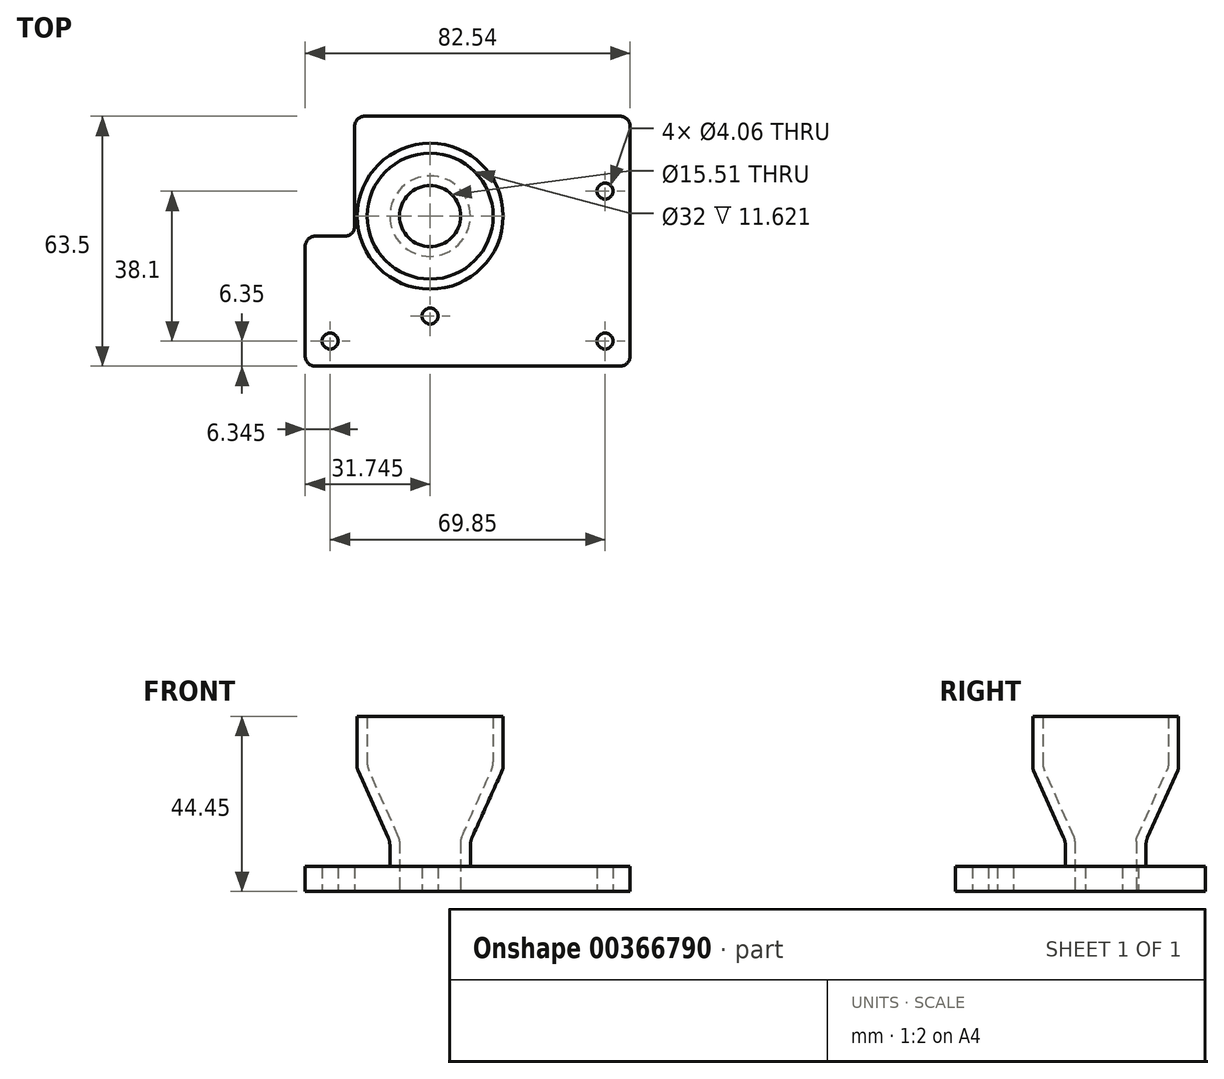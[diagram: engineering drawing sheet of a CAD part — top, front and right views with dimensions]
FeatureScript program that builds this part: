
annotation { "Feature Type Name" : "Feature", "Feature Type Description" : "" }
export const myFeature = defineFeature(function(context is Context, id is Id, definition is map)
    precondition{}
    {
        {
            var Q0;
            Q0=qCreatedBy(makeId("Top.planeOp"),FACE);
            var sketch = newSketch(context, id + "F0", { "sketchPlane" : qUnion([Q0])});
            skArc(sketch, "E0", {"start": v(-41.27, -29.21) * mm, "mid": v(-40.53, -31) * mm, "end": v(-38.73, -31.75) * mm});
            skCircle(sketch, "E1", {"center": v(-34.93, -25.4) * mm, "radius": 2.03 * mm});
            skLineSegment(sketch, "E2", {"start": v(-41.28, -1.3) * mm, "end": v(-41.28, -29.21) * mm});
            skArc(sketch, "E3", {"start": v(-38.73, 1.24) * mm, "mid": v(-40.53, 0.5) * mm, "end": v(-41.27, -1.3) * mm});
            skCircle(sketch, "E4", {"center": v(34.93, 12.7) * mm, "radius": 2.03 * mm});
            skCircle(sketch, "E5", {"center": v(34.93, -25.4) * mm, "radius": 2.03 * mm});
            skArc(sketch, "E6", {"start": v(38.74, -31.75) * mm, "mid": v(40.53, -31) * mm, "end": v(41.28, -29.21) * mm});
            skLineSegment(sketch, "E7", {"start": v(-38.73, -31.75) * mm, "end": v(38.74, -31.75) * mm});
            skCircle(sketch, "E8", {"center": v(-9.53, 6.35) * mm, "radius": 7.76 * mm});
            skLineSegment(sketch, "E9", {"start": v(41.28, -29.21) * mm, "end": v(41.28, 29.21) * mm});
            skArc(sketch, "E10", {"start": v(41.28, 29.21) * mm, "mid": v(40.53, 31) * mm, "end": v(38.74, 31.75) * mm});
            skCircle(sketch, "E11", {"center": v(-9.53, -19.05) * mm, "radius": 2.03 * mm});
            skLineSegment(sketch, "E12", {"start": v(-26.17, 31.75) * mm, "end": v(38.74, 31.75) * mm});
            skArc(sketch, "E13", {"start": v(-26.17, 31.75) * mm, "mid": v(-27.97, 31) * mm, "end": v(-28.7, 29.21) * mm});
            skLineSegment(sketch, "E14", {"start": v(-28.7, 3.78) * mm, "end": v(-28.7, 29.21) * mm});
            skLineSegment(sketch, "E15", {"start": v(-38.73, 1.24) * mm, "end": v(-31.25, 1.24) * mm});
            skArc(sketch, "E16", {"start": v(-31.25, 1.24) * mm, "mid": v(-29.45, 1.98) * mm, "end": v(-28.7, 3.78) * mm});
            skSolve(sketch);
        }
        {
            var Q0;
            Q0=makeQuery(id+"F0.imprint","IMPRINT",FACE,{"disambiguationData":[TD([[makeQuery(id+"F0.imprint","IMPRINT",EDGE,{"derivedFrom":sQuery(id+"F0.wireOp",EDGE,"E0")}),1.0]])]});
            extrude(context, id + "F1", {"entities" : qUnion([Q0]), "depth" : 6.35 * mm});
        }
        {
            var Q0;
            Q0=qCreatedBy(makeId("Top.planeOp"),FACE);
            cPlane(context, id + "F2", {"entities" : qUnion([Q0]), "cplaneType" : CPlaneType.OFFSET, "offset" : 6.35 * mm, "width" : 152.4 * mm, "height" : 152.4 * mm});
        }
        {
            var Q0;
            Q0=makeQuery(id+"F1.opExtrude","CAP_FACE",FACE,{"disambiguationData":[OSD([sQuery(id+"F0.wireOp",EDGE,"E0"),sQuery(id+"F0.wireOp",EDGE,"E1"),sQuery(id+"F0.wireOp",EDGE,"E2"),sQuery(id+"F0.wireOp",EDGE,"E3"),sQuery(id+"F0.wireOp",EDGE,"E4"),sQuery(id+"F0.wireOp",EDGE,"E5"),sQuery(id+"F0.wireOp",EDGE,"E6"),sQuery(id+"F0.wireOp",EDGE,"E7"),sQuery(id+"F0.wireOp",EDGE,"E8"),sQuery(id+"F0.wireOp",EDGE,"E9"),sQuery(id+"F0.wireOp",EDGE,"E10"),sQuery(id+"F0.wireOp",EDGE,"E11"),sQuery(id+"F0.wireOp",EDGE,"E12"),sQuery(id+"F0.wireOp",EDGE,"E13"),sQuery(id+"F0.wireOp",EDGE,"E14"),sQuery(id+"F0.wireOp",EDGE,"E15"),sQuery(id+"F0.wireOp",EDGE,"E16")])],"isStart":false});
            var sketch = newSketch(context, id + "F3", { "sketchPlane" : qUnion([Q0])});
            skCircle(sketch, "E17.0", {"center": v(-9.53, 6.35) * mm, "radius": 10.22 * mm});
            skCircle(sketch, "E18.0", {"center": v(-9.53, 6.35) * mm, "radius": 7.76 * mm});
            skSolve(sketch);
        }
        {
            var Q0;
            Q0 = qSketchRegion(id + "F3", true);
            extrude(context, id + "F4", {"entities" : qUnion([Q0]), "operationType" : NewBodyOperationType.ADD, "depth" : 6.35 * mm});
        }
        {
            var Q0;
            Q0=qCreatedBy(id+"F2.planeOp",FACE);
            cPlane(context, id + "F5", {"entities" : qUnion([Q0]), "cplaneType" : CPlaneType.OFFSET, "offset" : 25.4 * mm, "width" : 152.4 * mm, "height" : 152.4 * mm});
        }
        {
            var Q0;
            Q0=qCreatedBy(id+"F5.planeOp",FACE);
            var sketch = newSketch(context, id + "F6", { "sketchPlane" : qUnion([Q0])});
            skCircle(sketch, "E19", {"center": v(-9.53, 6.35) * mm, "radius": 18.54 * mm});
            skCircle(sketch, "E20.0", {"center": v(-9.53, 6.35) * mm, "radius": 16 * mm});
            skCircle(sketch, "E21.0", {"center": v(-9.53, 6.35) * mm, "radius": 7.76 * mm, "construction": true});
            skSolve(sketch);
        }
        {
            var Q0;
            Q0 = qSketchRegion(id + "F6", true);
            extrude(context, id + "F7", {"entities" : qUnion([Q0]), "depth" : 12.7 * mm});
        }
        {
            var Q0;
            Q0=makeQuery(id+"F7.opExtrude","CAP_FACE",FACE,{"disambiguationData":[OSD([sQuery(id+"F6.wireOp",EDGE,"E19"),sQuery(id+"F6.wireOp",EDGE,"E20.0")])],"isStart":false});
            var sketch = newSketch(context, id + "F8", { "sketchPlane" : qUnion([Q0])});
            skCircle(sketch, "E22.0", {"center": v(-9.53, 6.35) * mm, "radius": 16 * mm, "construction": true});
            skLineSegment(sketch, "E23", {"start": v(-9.53, 6.35) * mm, "end": v(6.47, 6.35) * mm, "construction": true});
            skSolve(sketch);
        }
        {
            var Q0;
            Q0=makeQuery(id+"F4.opExtrude","CAP_FACE",FACE,{"disambiguationData":[OSD([sQuery(id+"F3.wireOp",EDGE,"E17.0"),sQuery(id+"F3.wireOp",EDGE,"E18.0")])],"isStart":false});
            var sketch = newSketch(context, id + "F9", { "sketchPlane" : qUnion([Q0])});
            skCircle(sketch, "E24.0", {"center": v(-9.53, 6.35) * mm, "radius": 7.76 * mm, "construction": true});
            skLineSegment(sketch, "E25", {"start": v(-9.53, 6.35) * mm, "end": v(-1.77, 6.35) * mm, "construction": true});
            skSolve(sketch);
        }
        {
            var Q0;
            Q0=sQuery(id+"F8.wireOp",VERTEX,"E23.start");
            var Q1;
            Q1=sQuery(id+"F8.wireOp",VERTEX,"E23.end");
            var Q2;
            Q2=sQuery(id+"F9.wireOp",VERTEX,"E24.0.center");
            cPlane(context, id + "F10", {"entities" : qUnion([Q0, Q1, Q2]), "cplaneType" : CPlaneType.THREE_POINT, "offset" : 25.4 * mm, "width" : 152.4 * mm, "height" : 152.4 * mm});
        }
        {
            var Q0;
            Q0=qCreatedBy(id+"F10.planeOp",FACE);
            var sketch = newSketch(context, id + "F11", { "sketchPlane" : qUnion([Q0])});
            skLineSegment(sketch, "E26.0", {"start": v(-28.07, 44.45) * mm, "end": v(9.02, 44.45) * mm, "construction": true});
            skLineSegment(sketch, "E27.0", {"start": v(-25.52, 44.45) * mm, "end": v(6.47, 44.45) * mm, "construction": true});
            skLineSegment(sketch, "E28.0", {"start": v(-25.52, 31.75) * mm, "end": v(6.47, 31.75) * mm, "construction": true});
            skLineSegment(sketch, "E29.0", {"start": v(-28.07, 31.75) * mm, "end": v(9.02, 31.75) * mm, "construction": true});
            skLineSegment(sketch, "E30.0", {"start": v(-17.28, 12.7) * mm, "end": v(-1.77, 12.7) * mm, "construction": true});
            skLineSegment(sketch, "E31.0", {"start": v(-19.75, 12.7) * mm, "end": v(0.7, 12.7) * mm, "construction": true});
            skLineSegment(sketch, "E32", {"start": v(6.47, 31.75) * mm, "end": v(9.02, 31.75) * mm});
            skLineSegment(sketch, "E33", {"start": v(-1.77, 12.7) * mm, "end": v(0.7, 12.7) * mm});
            skLineSegment(sketch, "E34", {"start": v(-9.53, 44.45) * mm, "end": v(-9.53, 12.7) * mm, "construction": true});
            skArc(sketch, "E35", {"start": v(8.8, 30.7) * mm, "mid": v(8.96, 31.22) * mm, "end": v(9.02, 31.75) * mm});
            skArc(sketch, "E36", {"start": v(-1.55, 13.7) * mm, "mid": v(-1.71, 13.21) * mm, "end": v(-1.77, 12.7) * mm});
            skLineSegment(sketch, "E37", {"start": v(-1.77, 13.22) * mm, "end": v(6.48, 31.75) * mm});
            skLineSegment(sketch, "E38", {"start": v(0.7, 12.7) * mm, "end": v(8.8, 30.7) * mm});
            skSolve(sketch);
        }
        {
            var Q0;
            {var subQ1=sQuery(id+"F11.wireOp",EDGE,"E32");Q0=makeQuery(id+"F11.imprint","IMPRINT",FACE,{"disambiguationData":[TD([[makeQuery(id+"F11.imprint","IMPRINT",EDGE,{"derivedFrom":subQ1}),-1.0]])]});}
            var Q1;
            Q1=sQuery(id+"F11.wireOp",EDGE,"E34");
            revolve(context, id + "F12", {"operationType" : NewBodyOperationType.ADD, "entities" : qUnion([Q0]), "axis" : qUnion([Q1]), "revolveType" : RevolveType.FULL});
        }
        {
            var Q0;
            Q0=makeQuery(id+"F12.boolean.opBoolean","MERGE",EDGE,{"derivedFrom":[makeQuery(id+"F4.opExtrude","CAP_EDGE",EDGE,{"disambiguationData":[OSD([sQuery(id+"F3.wireOp",EDGE,"E17.0")])],"isStart":false}),makeQuery(id+"F12.opRevolve","SWEPT_EDGE",EDGE,{"disambiguationData":[OSD([sQuery(id+"F11.wireOp",EDGE,"E33"),sQuery(id+"F11.wireOp",EDGE,"E38")])]})]});
            var Q1;
            Q1=makeQuery(id+"F4.opExtrude","CAP_EDGE",EDGE,{"disambiguationData":[OSD([sQuery(id+"F3.wireOp",EDGE,"E17.0")])],"isStart":true});
            var Q2;
            Q2=makeQuery(id+"F12.boolean.opBoolean","MERGE",EDGE,{"derivedFrom":[makeQuery(id+"F7.opExtrude","CAP_EDGE",EDGE,{"disambiguationData":[OSD([sQuery(id+"F6.wireOp",EDGE,"E20.0")])],"isStart":true}),makeQuery(id+"F12.opRevolve","SWEPT_EDGE",EDGE,{"disambiguationData":[OSD([sQuery(id+"F11.wireOp",EDGE,"E32"),sQuery(id+"F11.wireOp",EDGE,"E37")])]})]});
            fillet(context, id + "F13", {"entities" : qUnion([Q0, Q1, Q2]), "radius" : 5.08 * mm, "tangentPropagation" : true, "allowEdgeOverflow" : false});
        }
    });
